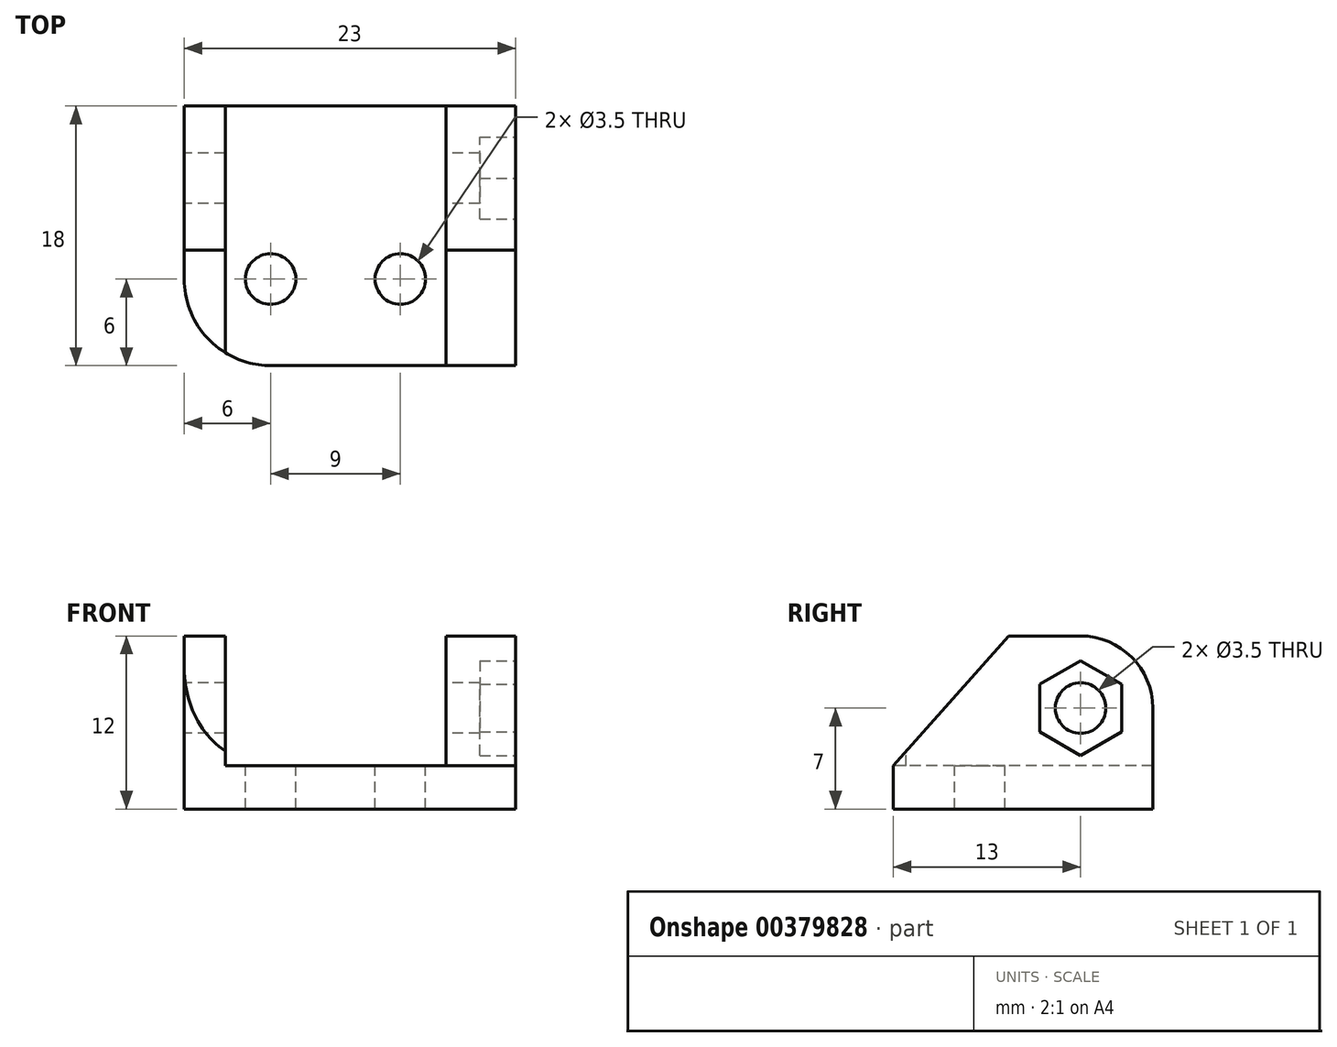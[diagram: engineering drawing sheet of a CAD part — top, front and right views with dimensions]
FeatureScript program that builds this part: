
annotation { "Feature Type Name" : "Feature", "Feature Type Description" : "" }
export const myFeature = defineFeature(function(context is Context, id is Id, definition is map)
    precondition{}
    {
        {
            var Q0;
            Q0=qCreatedBy(makeId("Top.planeOp"),FACE);
            var sketch = newSketch(context, id + "F0", { "sketchPlane" : qUnion([Q0])});
            skLineSegment(sketch, "E0.bottom", {"start": v(0, 0) * mm, "end": v(21, 0) * mm});
            skLineSegment(sketch, "E0.top", {"start": v(0, 18) * mm, "end": v(21, 18) * mm});
            skLineSegment(sketch, "E0.left", {"start": v(0, 0) * mm, "end": v(0, 18) * mm});
            skLineSegment(sketch, "E0.right", {"start": v(21, 0) * mm, "end": v(21, 18) * mm});
            skSolve(sketch);
        }
        {
            var Q0;
            Q0=qSketchRegion(id+"F0",true);
            extrude(context, id + "F1", {"entities" : qUnion([Q0]), "depth" : 3 * mm});
        }
        {
            var Q0;
            Q0=makeQuery(id+"F1.opExtrude","CAP_FACE",FACE,{"disambiguationData":[OSD([sQuery(id+"F0.wireOp",EDGE,"E0.bottom"),sQuery(id+"F0.wireOp",EDGE,"E0.top"),sQuery(id+"F0.wireOp",EDGE,"E0.left"),sQuery(id+"F0.wireOp",EDGE,"E0.right")])],"isStart":false});
            var sketch = newSketch(context, id + "F2", { "sketchPlane" : qUnion([Q0])});
            skLineSegment(sketch, "E1.bottom", {"start": v(0, 18) * mm, "end": v(2.85, 18) * mm});
            skLineSegment(sketch, "E1.top", {"start": v(0, 0) * mm, "end": v(2.85, 0) * mm});
            skLineSegment(sketch, "E1.left", {"start": v(0, 18) * mm, "end": v(0, 0) * mm});
            skLineSegment(sketch, "E1.right", {"start": v(2.85, 18) * mm, "end": v(2.85, 0) * mm});
            skLineSegment(sketch, "E2.bottom", {"start": v(21, 18) * mm, "end": v(18.15, 18) * mm});
            skLineSegment(sketch, "E2.top", {"start": v(21, 0) * mm, "end": v(18.15, 0) * mm});
            skLineSegment(sketch, "E2.left", {"start": v(21, 18) * mm, "end": v(21, 0) * mm});
            skLineSegment(sketch, "E2.right", {"start": v(18.15, 18) * mm, "end": v(18.15, 0) * mm});
            skSolve(sketch);
        }
        {
            var Q0;
            Q0=qSketchRegion(id+"F2",true);
            extrude(context, id + "F3", {"entities" : qUnion([Q0]), "operationType" : NewBodyOperationType.ADD, "depth" : 9 * mm});
        }
        {
            var Q0;
            Q0=makeQuery(id+"F3.boolean.opBoolean","MERGE",EDGE,{"derivedFrom":[makeQuery(id+"F1.opExtrude","SWEPT_EDGE",EDGE,{"disambiguationData":[OSD([sQuery(id+"F0.wireOp",EDGE,"E0.bottom"),sQuery(id+"F0.wireOp",EDGE,"E0.left")])]}),makeQuery(id+"F3.opExtrude","SWEPT_EDGE",EDGE,{"disambiguationData":[OSD([sQuery(id+"F2.wireOp",EDGE,"E1.top"),sQuery(id+"F2.wireOp",EDGE,"E1.left")])]})]});
            fillet(context, id + "F4", {"entities" : qUnion([Q0]), "radius" : 6 * mm, "tangentPropagation" : true, "allowEdgeOverflow" : false});
        }
        {
            var Q0;
            Q0=makeQuery(id+"F3.boolean.opBoolean","MERGE",FACE,{"derivedFrom":[makeQuery(id+"F1.opExtrude","SWEPT_FACE",FACE,{"disambiguationData":[OSD([sQuery(id+"F0.wireOp",EDGE,"E0.left")])]}),makeQuery(id+"F3.opExtrude","SWEPT_FACE",FACE,{"disambiguationData":[OSD([sQuery(id+"F2.wireOp",EDGE,"E1.left")])]})]});
            var sketch = newSketch(context, id + "F5", { "sketchPlane" : qUnion([Q0])});
            skCircle(sketch, "E3", {"center": v(-13, 7) * mm, "radius": 1.75 * mm});
            skLineSegment(sketch, "E4.0.1", {"start": v(0, 0) * mm, "end": v(0, 12) * mm, "construction": true});
            skLineSegment(sketch, "E4.0.3", {"start": v(0, 12) * mm, "end": v(0, 3) * mm, "construction": true});
            skLineSegment(sketch, "E5", {"start": v(-8, 12) * mm, "end": v(0, 3) * mm});
            skLineSegment(sketch, "E6", {"start": v(0, 16.5) * mm, "end": v(0, 3) * mm});
            skLineSegment(sketch, "E7.0.0", {"start": v(-18, 3) * mm, "end": v(0, 3) * mm, "construction": true});
            skLineSegment(sketch, "E7.0.1", {"start": v(0, 3) * mm, "end": v(0, 12) * mm, "construction": true});
            skLineSegment(sketch, "E7.0.2", {"start": v(0, 12) * mm, "end": v(-18, 12) * mm, "construction": true});
            skLineSegment(sketch, "E7.0.3", {"start": v(-18, 12) * mm, "end": v(-18, 3) * mm, "construction": true});
            skLineSegment(sketch, "E8", {"start": v(-8, 12) * mm, "end": v(0, 12) * mm});
            skLineSegment(sketch, "E9", {"start": v(0, 12) * mm, "end": v(0, 3) * mm});
            skSolve(sketch);
        }
        {
            var Q0;
            Q0=qSketchRegion(id+"F5",true);
            extrude(context, id + "F6", {"entities" : qUnion([Q0]), "operationType" : NewBodyOperationType.REMOVE, "endBound" : BoundingType.THROUGH_ALL, "oppositeDirection" : true, "depth" : 25 * mm});
        }
        {
            var Q0;
            Q0=makeQuery(id+"F3.opExtrude","CAP_EDGE",EDGE,{"disambiguationData":[OSD([sQuery(id+"F2.wireOp",EDGE,"E1.bottom")])],"isStart":false});
            var Q1;
            Q1=makeQuery(id+"F3.opExtrude","CAP_EDGE",EDGE,{"disambiguationData":[OSD([sQuery(id+"F2.wireOp",EDGE,"E2.bottom")])],"isStart":false});
            var Q2;
            {var subQ0=sQuery(id+"F2.wireOp",EDGE,"E1.left");var subQ1=sQuery(id+"F5.wireOp",EDGE,"E5");Q2=makeQuery(id+"F6.boolean.opBoolean","COPY",EDGE,{"disambiguationData":[topologyDisambiguationEdgeConnected([makeQuery(id+"F3.opExtrude","CAP_FACE",FACE,{"disambiguationData":[OSD([sQuery(id+"F2.wireOp",EDGE,"E1.bottom"),sQuery(id+"F2.wireOp",EDGE,"E1.top"),subQ0,sQuery(id+"F2.wireOp",EDGE,"E1.right")])],"isStart":false})])],"derivedFrom":makeQuery(id+"F6.opExtrude","SWEPT_EDGE",EDGE,{"disambiguationData":[OSD([subQ0,sQuery(id+"F5.wireOp",EDGE,"toCVR1km-wCAx-B5Tf-Qxij-KXW5aZ6ogp7M"),subQ1])]})});}
            var Q3;
            {var subQ0=sQuery(id+"F5.wireOp",EDGE,"E5");Q3=makeQuery(id+"F6.boolean.opBoolean","COPY",EDGE,{"disambiguationData":[topologyDisambiguationEdgeConnected([makeQuery(id+"F3.opExtrude","CAP_FACE",FACE,{"disambiguationData":[OSD([sQuery(id+"F2.wireOp",EDGE,"E2.bottom"),sQuery(id+"F2.wireOp",EDGE,"E2.top"),sQuery(id+"F2.wireOp",EDGE,"E2.left"),sQuery(id+"F2.wireOp",EDGE,"E2.right")])],"isStart":false})])],"derivedFrom":makeQuery(id+"F6.opExtrude","SWEPT_EDGE",EDGE,{"disambiguationData":[OSD([sQuery(id+"F2.wireOp",EDGE,"E1.left"),sQuery(id+"F5.wireOp",EDGE,"toCVR1km-wCAx-B5Tf-Qxij-KXW5aZ6ogp7M"),subQ0])]})});}
            var Q4;
            {var subQ0=sQuery(id+"F2.wireOp",EDGE,"E1.top");var subQ1=sQuery(id+"F0.wireOp",EDGE,"E0.left");var subQ2=sQuery(id+"F0.wireOp",EDGE,"E0.bottom");var subQ3=sQuery(id+"F2.wireOp",EDGE,"E1.left");var subQ4=sQuery(id+"F5.wireOp",EDGE,"E5");Q4=makeQuery(id+"F6.boolean.opBoolean","COPY",EDGE,{"disambiguationData":[TD([makeQuery(id+"F1.opExtrude","SWEPT_FACE",FACE,{"disambiguationData":[OSD([subQ1])]})])],"derivedFrom":makeQuery(id+"F6.opExtrude","SWEPT_EDGE",EDGE,{"disambiguationData":[OSD([subQ2,subQ1,subQ0,subQ3,subQ4,sQuery(id+"F5.wireOp",EDGE,"E6")])]})});}
            fillet(context, id + "F7", {"entities" : qUnion([Q0, Q1, Q2, Q3, Q4]), "radius" : 5 * mm, "tangentPropagation" : true, "allowEdgeOverflow" : false});
        }
        {
            var Q0;
            Q0=makeQuery(id+"F1.opExtrude","CAP_FACE",FACE,{"disambiguationData":[OSD([sQuery(id+"F0.wireOp",EDGE,"E0.bottom"),sQuery(id+"F0.wireOp",EDGE,"E0.top"),sQuery(id+"F0.wireOp",EDGE,"E0.left"),sQuery(id+"F0.wireOp",EDGE,"E0.right")])],"isStart":false});
            var sketch = newSketch(context, id + "F8", { "sketchPlane" : qUnion([Q0])});
            skCircle(sketch, "E10", {"center": v(6, 6) * mm, "radius": 1.75 * mm});
            skCircle(sketch, "E11", {"center": v(15, 6) * mm, "radius": 1.75 * mm});
            skSolve(sketch);
        }
        {
            var Q0;
            Q0=qSketchRegion(id+"F8",true);
            extrude(context, id + "F9", {"entities" : qUnion([Q0]), "operationType" : NewBodyOperationType.REMOVE, "endBound" : BoundingType.THROUGH_ALL, "oppositeDirection" : true, "depth" : 25 * mm});
        }
        {
            var Q0;
            Q0=makeQuery(id+"F3.boolean.opBoolean","MERGE",FACE,{"derivedFrom":[makeQuery(id+"F1.opExtrude","SWEPT_FACE",FACE,{"disambiguationData":[OSD([sQuery(id+"F0.wireOp",EDGE,"E0.right")])]}),makeQuery(id+"F3.opExtrude","SWEPT_FACE",FACE,{"disambiguationData":[OSD([sQuery(id+"F2.wireOp",EDGE,"E2.left")])]})]});
            extrude(context, id + "F10", {"entities" : qUnion([Q0]), "operationType" : NewBodyOperationType.ADD, "depth" : 2 * mm});
        }
        {
            var Q0;
            Q0=makeQuery(id+"F10.opExtrude","CAP_FACE",FACE,{"disambiguationData":[OSD([sQuery(id+"F0.wireOp",EDGE,"E0.right"),sQuery(id+"F2.wireOp",EDGE,"E2.left")])],"isStart":false});
            var sketch = newSketch(context, id + "F11", { "sketchPlane" : qUnion([Q0])});
            skCircle(sketch, "E12.cCircle", {"center": v(13, 7) * mm, "radius": 2.85 * mm, "construction": true});
            skLineSegment(sketch, "E12.0", {"start": v(15.85, 8.65) * mm, "end": v(15.85, 5.35) * mm});
            skLineSegment(sketch, "E12.1", {"start": v(15.85, 5.35) * mm, "end": v(13, 3.7) * mm});
            skLineSegment(sketch, "E12.2", {"start": v(13, 3.7) * mm, "end": v(10.15, 5.35) * mm});
            skLineSegment(sketch, "E12.3", {"start": v(10.15, 5.35) * mm, "end": v(10.15, 8.65) * mm});
            skLineSegment(sketch, "E12.4", {"start": v(10.15, 8.65) * mm, "end": v(13, 10.3) * mm});
            skLineSegment(sketch, "E12.5", {"start": v(13, 10.3) * mm, "end": v(15.85, 8.65) * mm});
            skPoint(sketch, "E12.0.midPoint", {"position": v(15.85, 7) * mm});
            skSolve(sketch);
        }
        {
            var Q0;
            Q0=qSketchRegion(id+"F11",true);
            extrude(context, id + "F12", {"entities" : qUnion([Q0]), "operationType" : NewBodyOperationType.REMOVE, "oppositeDirection" : true, "depth" : 2.5 * mm});
        }
    });
